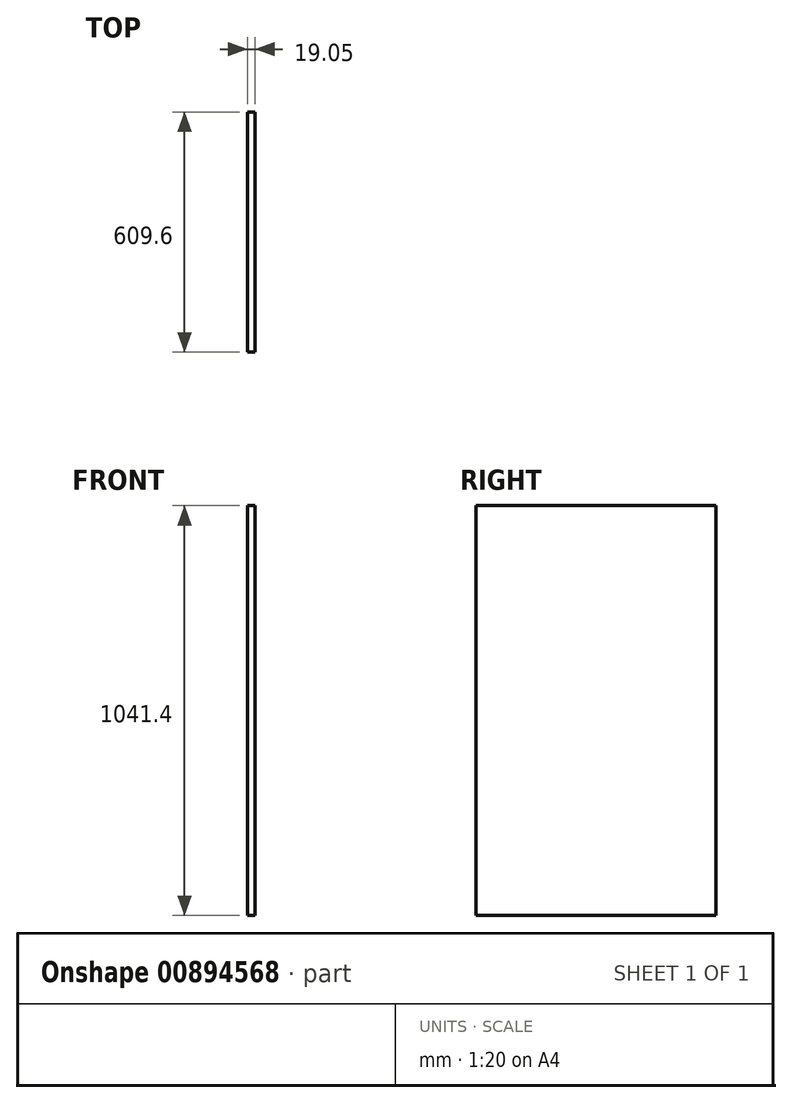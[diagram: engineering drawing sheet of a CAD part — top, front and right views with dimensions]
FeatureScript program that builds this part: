
annotation { "Feature Type Name" : "Feature", "Feature Type Description" : "" }
export const myFeature = defineFeature(function(context is Context, id is Id, definition is map)
    precondition{}
    {
        {
            var Q0;
            Q0=qCreatedBy(makeId("Right.planeOp"),FACE);
            var sketch = newSketch(context, id + "F0", { "sketchPlane" : qUnion([Q0])});
            skLineSegment(sketch, "E0.bottom", {"start": v(304.8, 520.7) * mm, "end": v(-304.8, 520.7) * mm});
            skLineSegment(sketch, "E0.top", {"start": v(304.8, -520.7) * mm, "end": v(-304.8, -520.7) * mm});
            skLineSegment(sketch, "E0.left", {"start": v(304.8, 520.7) * mm, "end": v(304.8, -520.7) * mm});
            skLineSegment(sketch, "E0.right", {"start": v(-304.8, 520.7) * mm, "end": v(-304.8, -520.7) * mm});
            skPoint(sketch, "E0.middle", {"position": v(0, 0) * mm});
            skSolve(sketch);
        }
        {
            var Q0;
            Q0=makeQuery(id+"F0.imprint","IMPRINT",FACE,{"disambiguationData":[TD([[makeQuery(id+"F0.imprint","IMPRINT",EDGE,{"derivedFrom":sQuery(id+"F0.wireOp",EDGE,"E0.top")}),-1.0]])]});
            extrude(context, id + "F1", {"entities" : qUnion([Q0]), "depth" : 19.05 * mm, "offsetDistance" : 25.4 * mm});
        }
    });
